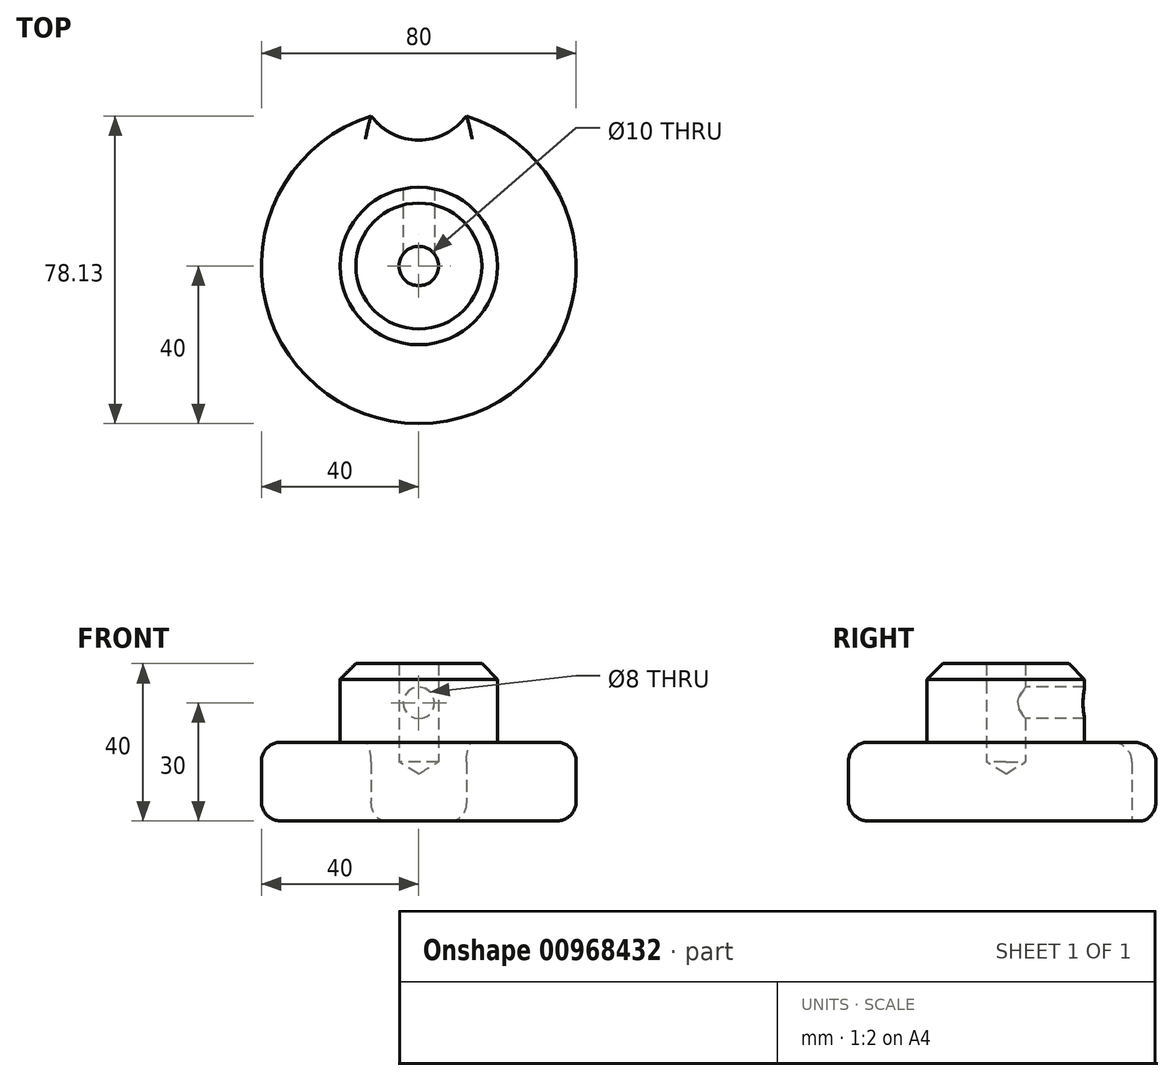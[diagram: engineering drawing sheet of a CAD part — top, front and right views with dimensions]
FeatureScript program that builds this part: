
annotation { "Feature Type Name" : "Feature", "Feature Type Description" : "" }
export const myFeature = defineFeature(function(context is Context, id is Id, definition is map)
    precondition{}
    {
        {
            var Q0;
            Q0=qCreatedBy(makeId("Front.planeOp"),FACE);
            var sketch = newSketch(context, id + "F0", { "sketchPlane" : qUnion([Q0])});
            skLineSegment(sketch, "E0", {"start": v(0, 0) * mm, "end": v(40, 0) * mm});
            skLineSegment(sketch, "E1", {"start": v(40, 0) * mm, "end": v(40, 20) * mm});
            skLineSegment(sketch, "E2", {"start": v(40, 20) * mm, "end": v(20, 20) * mm});
            skLineSegment(sketch, "E3", {"start": v(20, 20) * mm, "end": v(20, 40) * mm});
            skLineSegment(sketch, "E4", {"start": v(20, 40) * mm, "end": v(0, 40) * mm});
            skLineSegment(sketch, "E5", {"start": v(0, 40) * mm, "end": v(0, 0) * mm});
            skSolve(sketch);
        }
        {
            var Q0;
            Q0=qCreatedBy(makeId("Top.planeOp"),FACE);
            var sketch = newSketch(context, id + "F1", { "sketchPlane" : qUnion([Q0])});
            skCircle(sketch, "E6", {"center": v(0, 47) * mm, "radius": 15 * mm});
            skSolve(sketch);
        }
        {
            var Q0;
            Q0=makeQuery(id+"F0.imprint","IMPRINT",FACE,{"disambiguationData":[TD([[makeQuery(id+"F0.imprint","IMPRINT",EDGE,{"derivedFrom":sQuery(id+"F0.wireOp",EDGE,"E0")}),1.0]])]});
            var Q1;
            Q1=sQuery(id+"F0.wireOp",EDGE,"E5");
            revolve(context, id + "F2", {"surfaceOperationType" : NewSurfaceOperationType.NEW, "entities" : qUnion([Q0]), "axis" : qUnion([Q1]), "revolveType" : RevolveType.FULL});
        }
        {
            var Q0;
            Q0=makeQuery(id+"F2.opRevolve","SWEPT_EDGE",EDGE,{"disambiguationData":[OSD([sQuery(id+"F0.wireOp",EDGE,"E3"),sQuery(id+"F0.wireOp",EDGE,"E4")])]});
            chamfer(context, id + "F3", {"entities" : qUnion([Q0]), "width" : 4 * mm, "tangentPropagation" : true});
        }
        {
            var Q0;
            Q0=makeQuery(id+"F2.opRevolve","SWEPT_FACE",FACE,{"disambiguationData":[OSD([sQuery(id+"F0.wireOp",EDGE,"E4")])]});
            var sketch = newSketch(context, id + "F4", { "sketchPlane" : qUnion([Q0])});
            skPoint(sketch, "E7.0", {"position": v(0, 0) * mm});
            skSolve(sketch);
        }
        {
            var Q0;
            Q0=sQuery(id+"F4.wireOp",VERTEX,"E7.0");
            var Q1;
            Q1=makeQuery(id+"F2.opRevolve","SWEPT_BODY",BODY,{"disambiguationData":[OSD([sQuery(id+"F0.wireOp",EDGE,"E0"),sQuery(id+"F0.wireOp",EDGE,"E1"),sQuery(id+"F0.wireOp",EDGE,"E2"),sQuery(id+"F0.wireOp",EDGE,"E3"),sQuery(id+"F0.wireOp",EDGE,"E4"),sQuery(id+"F0.wireOp",EDGE,"E5")])]});
            hole(context, id + "F5", {"style" : HoleStyle.SIMPLE, "endStyle" : HoleEndStyle.BLIND, "holeDiameter" : 10 * mm, "majorDiameter" : 5 * mm, "holeDepth" : 25 * mm, "isTappedThrough" : true, "tappedDepth" : 22 * mm, "tapClearance" : 0, "startFromSketch" : true, "locations" : qUnion([Q0]), "scope" : qUnion([Q1])});
        }
        {
            var Q0;
            Q0=makeQuery(id+"F1.imprint","IMPRINT",FACE,{"disambiguationData":[TD([[makeQuery(id+"F1.imprint","IMPRINT",EDGE,{"derivedFrom":sQuery(id+"F1.wireOp",EDGE,"E6")}),1.0]])]});
            extrude(context, id + "F6", {"entities" : qUnion([Q0]), "operationType" : NewBodyOperationType.REMOVE, "endBound" : BoundingType.THROUGH_ALL, "depth" : 25 * mm, "offsetDistance" : 25 * mm});
        }
        {
            var Q0;
            Q0=makeQuery(id+"F2.opRevolve","SWEPT_EDGE",EDGE,{"disambiguationData":[OSD([sQuery(id+"F0.wireOp",EDGE,"E1"),sQuery(id+"F0.wireOp",EDGE,"E2")])]});
            var Q1;
            Q1=makeQuery(id+"F2.opRevolve","SWEPT_EDGE",EDGE,{"disambiguationData":[OSD([sQuery(id+"F0.wireOp",EDGE,"E0"),sQuery(id+"F0.wireOp",EDGE,"E1")])]});
            var Q2;
            Q2=makeQuery(id+"FCN2Jhjehv3hhp9_1.2.F6.boolean.opBoolean","INTERSECT",EDGE,{"derivedFrom":[makeQuery(id+"F2.opRevolve","SWEPT_FACE",FACE,{"disambiguationData":[OSD([sQuery(id+"F0.wireOp",EDGE,"E2")])]}),makeQuery(id+"FCN2Jhjehv3hhp9_1.2.F6.opExtrude","SWEPT_FACE",FACE,{"disambiguationData":[OSD([sQuery(id+"F1.wireOp",EDGE,"E6")])]})]});
            var Q3;
            Q3=makeQuery(id+"FCN2Jhjehv3hhp9_1.2.F6.boolean.opBoolean","COPY",EDGE,{"derivedFrom":makeQuery(id+"FCN2Jhjehv3hhp9_1.2.F6.opExtrude","CAP_EDGE",EDGE,{"disambiguationData":[OSD([sQuery(id+"F1.wireOp",EDGE,"E6")])],"isStart":true})});
            var Q4;
            Q4=makeQuery(id+"FCN2Jhjehv3hhp9_1.3.F6.boolean.opBoolean","COPY",EDGE,{"derivedFrom":makeQuery(id+"FCN2Jhjehv3hhp9_1.3.F6.opExtrude","CAP_EDGE",EDGE,{"disambiguationData":[OSD([sQuery(id+"F1.wireOp",EDGE,"E6")])],"isStart":true})});
            var Q5;
            Q5=makeQuery(id+"FCN2Jhjehv3hhp9_1.3.F6.boolean.opBoolean","INTERSECT",EDGE,{"derivedFrom":[makeQuery(id+"F2.opRevolve","SWEPT_FACE",FACE,{"disambiguationData":[OSD([sQuery(id+"F0.wireOp",EDGE,"E2")])]}),makeQuery(id+"FCN2Jhjehv3hhp9_1.3.F6.opExtrude","SWEPT_FACE",FACE,{"disambiguationData":[OSD([sQuery(id+"F1.wireOp",EDGE,"E6")])]})]});
            var Q6;
            Q6=makeQuery(id+"FCN2Jhjehv3hhp9_1.1.F6.boolean.opBoolean","COPY",EDGE,{"derivedFrom":makeQuery(id+"FCN2Jhjehv3hhp9_1.1.F6.opExtrude","CAP_EDGE",EDGE,{"disambiguationData":[OSD([sQuery(id+"F1.wireOp",EDGE,"E6")])],"isStart":true})});
            var Q7;
            Q7=makeQuery(id+"FCN2Jhjehv3hhp9_1.4.F6.boolean.opBoolean","COPY",EDGE,{"derivedFrom":makeQuery(id+"FCN2Jhjehv3hhp9_1.4.F6.opExtrude","CAP_EDGE",EDGE,{"disambiguationData":[OSD([sQuery(id+"F1.wireOp",EDGE,"E6")])],"isStart":true})});
            var Q8;
            Q8=makeQuery(id+"FCN2Jhjehv3hhp9_1.5.F6.boolean.opBoolean","COPY",EDGE,{"derivedFrom":makeQuery(id+"FCN2Jhjehv3hhp9_1.5.F6.opExtrude","CAP_EDGE",EDGE,{"disambiguationData":[OSD([sQuery(id+"F1.wireOp",EDGE,"E6")])],"isStart":true})});
            var Q9;
            Q9=makeQuery(id+"F6.boolean.opBoolean","COPY",EDGE,{"derivedFrom":makeQuery(id+"F6.opExtrude","CAP_EDGE",EDGE,{"disambiguationData":[OSD([sQuery(id+"F1.wireOp",EDGE,"E6")])],"isStart":true})});
            var Q10;
            Q10=makeQuery(id+"FCN2Jhjehv3hhp9_1.1.F6.boolean.opBoolean","INTERSECT",EDGE,{"derivedFrom":[makeQuery(id+"F2.opRevolve","SWEPT_FACE",FACE,{"disambiguationData":[OSD([sQuery(id+"F0.wireOp",EDGE,"E2")])]}),makeQuery(id+"FCN2Jhjehv3hhp9_1.1.F6.opExtrude","SWEPT_FACE",FACE,{"disambiguationData":[OSD([sQuery(id+"F1.wireOp",EDGE,"E6")])]})]});
            var Q11;
            Q11=makeQuery(id+"F6.boolean.opBoolean","INTERSECT",EDGE,{"derivedFrom":[makeQuery(id+"F2.opRevolve","SWEPT_FACE",FACE,{"disambiguationData":[OSD([sQuery(id+"F0.wireOp",EDGE,"E2")])]}),makeQuery(id+"F6.opExtrude","SWEPT_FACE",FACE,{"disambiguationData":[OSD([sQuery(id+"F1.wireOp",EDGE,"E6")])]})]});
            var Q12;
            Q12=makeQuery(id+"FCN2Jhjehv3hhp9_1.5.F6.boolean.opBoolean","INTERSECT",EDGE,{"derivedFrom":[makeQuery(id+"F2.opRevolve","SWEPT_FACE",FACE,{"disambiguationData":[OSD([sQuery(id+"F0.wireOp",EDGE,"E2")])]}),makeQuery(id+"FCN2Jhjehv3hhp9_1.5.F6.opExtrude","SWEPT_FACE",FACE,{"disambiguationData":[OSD([sQuery(id+"F1.wireOp",EDGE,"E6")])]})]});
            var Q13;
            Q13=makeQuery(id+"FCN2Jhjehv3hhp9_1.4.F6.boolean.opBoolean","INTERSECT",EDGE,{"derivedFrom":[makeQuery(id+"F2.opRevolve","SWEPT_FACE",FACE,{"disambiguationData":[OSD([sQuery(id+"F0.wireOp",EDGE,"E2")])]}),makeQuery(id+"FCN2Jhjehv3hhp9_1.4.F6.opExtrude","SWEPT_FACE",FACE,{"disambiguationData":[OSD([sQuery(id+"F1.wireOp",EDGE,"E6")])]})]});
            fillet(context, id + "F7", {"entities" : qUnion([Q0, Q1, Q2, Q3, Q4, Q5, Q6, Q7, Q8, Q9, Q10, Q11, Q12, Q13]), "radius" : 5 * mm, "tangentPropagation" : true, "allowEdgeOverflow" : false});
        }
        {
            var Q0;
            Q0=qCreatedBy(makeId("Front.planeOp"),FACE);
            var sketch = newSketch(context, id + "F8", { "sketchPlane" : qUnion([Q0])});
            skCircle(sketch, "E8", {"center": v(0, 30) * mm, "radius": 4 * mm});
            skSolve(sketch);
        }
        {
            var Q0;
            Q0 = qSketchRegion(id + "F8", true);
            extrude(context, id + "F9", {"entities" : qUnion([Q0]), "operationType" : NewBodyOperationType.REMOVE, "endBound" : BoundingType.THROUGH_ALL, "oppositeDirection" : true, "depth" : 25 * mm, "offsetDistance" : 25 * mm});
        }
    });
